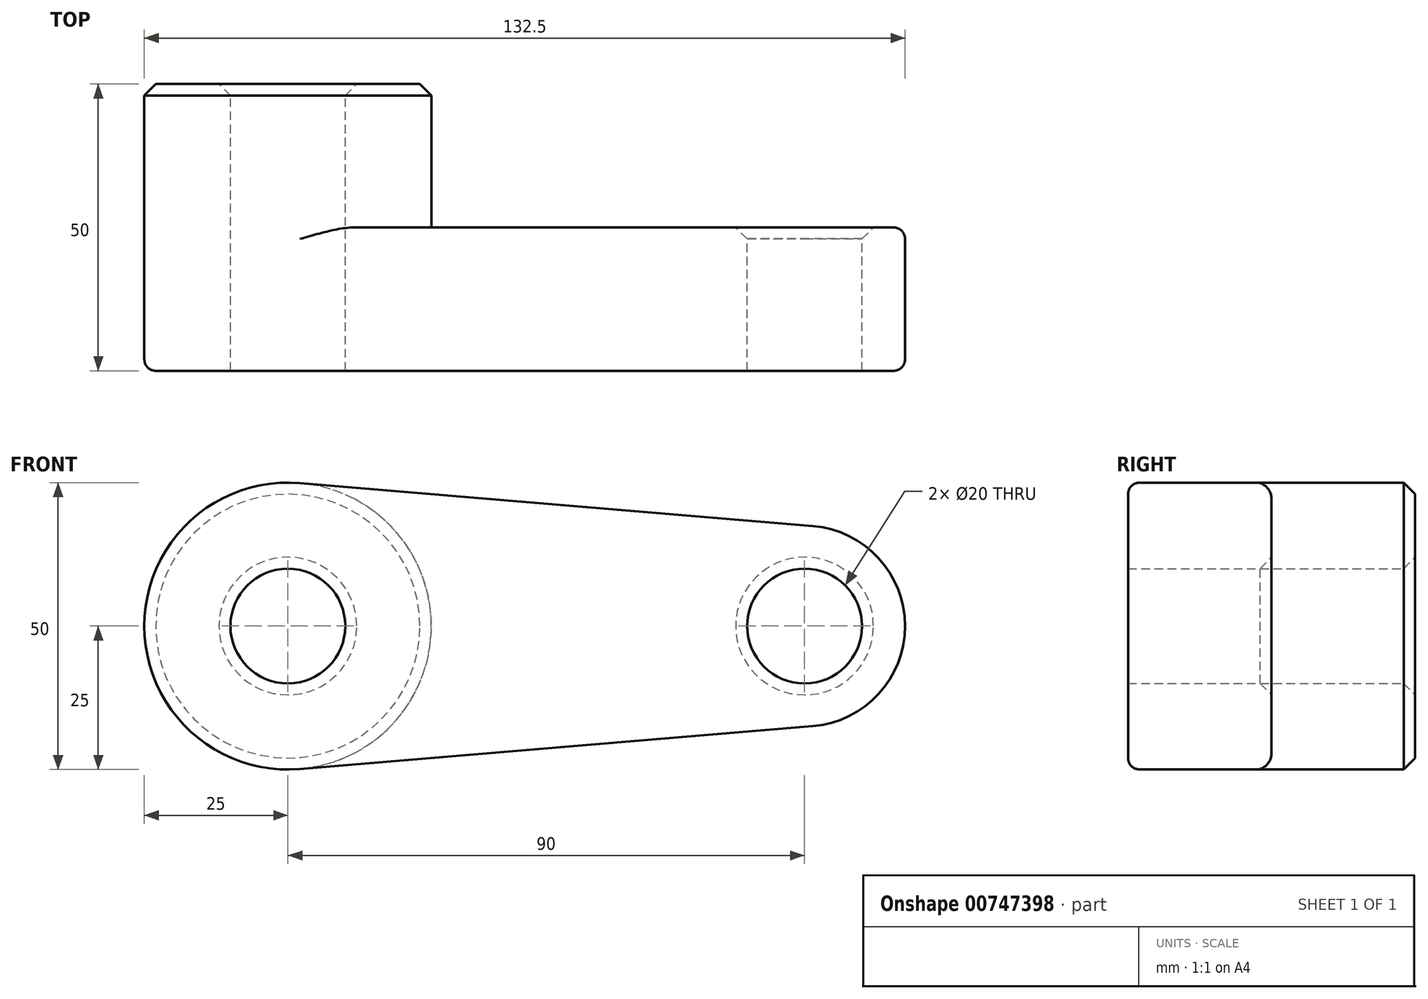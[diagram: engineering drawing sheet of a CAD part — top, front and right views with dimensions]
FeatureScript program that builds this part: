
annotation { "Feature Type Name" : "Feature", "Feature Type Description" : "" }
export const myFeature = defineFeature(function(context is Context, id is Id, definition is map)
    precondition{}
    {
        {
            var Q0;
            Q0=qCreatedBy(makeId("Front.planeOp"),FACE);
            var sketch = newSketch(context, id + "F0", { "sketchPlane" : qUnion([Q0])});
            skCircle(sketch, "E0", {"center": v(0, 0) * mm, "radius": 25 * mm});
            skCircle(sketch, "E1", {"center": v(90, 0) * mm, "radius": 17.5 * mm});
            skLineSegment(sketch, "E2", {"start": v(2.08, 24.91) * mm, "end": v(91.46, 17.44) * mm});
            skLineSegment(sketch, "E3", {"start": v(2.08, -24.91) * mm, "end": v(91.46, -17.44) * mm});
            skCircle(sketch, "E4", {"center": v(0, 0) * mm, "radius": 10 * mm});
            skCircle(sketch, "E5", {"center": v(90, 0) * mm, "radius": 10 * mm});
            skSolve(sketch);
        }
        {
            var Q0;
            Q0 = qSketchRegion(id + "F0", true);
            extrude(context, id + "F1", {"entities" : qUnion([Q0]), "depth" : 25 * mm, "offsetDistance" : 25 * mm});
        }
        {
            var Q0;
            Q0=makeQuery(id+"F0.imprint","IMPRINT",FACE,{"disambiguationData":[TD([[makeQuery(id+"F0.imprint","IMPRINT",EDGE,{"derivedFrom":sQuery(id+"F0.wireOp",EDGE,"E4")}),-1.0]])]});
            extrude(context, id + "F2", {"entities" : qUnion([Q0]), "operationType" : NewBodyOperationType.ADD, "oppositeDirection" : true, "depth" : 25 * mm, "offsetDistance" : 25 * mm});
        }
        {
            var Q0;
            Q0=makeQuery(id+"F2.opExtrude","CAP_EDGE",EDGE,{"disambiguationData":[OSD([sQuery(id+"F0.wireOp",EDGE,"E0")])],"isStart":false});
            var Q1;
            Q1=makeQuery(id+"F2.opExtrude","CAP_EDGE",EDGE,{"disambiguationData":[OSD([sQuery(id+"F0.wireOp",EDGE,"E4")])],"isStart":false});
            var Q2;
            Q2=makeQuery(id+"F1.opExtrude","CAP_EDGE",EDGE,{"disambiguationData":[OSD([sQuery(id+"F0.wireOp",EDGE,"E5")])],"isStart":true});
            chamfer(context, id + "F3", {"entities" : qUnion([Q0, Q1, Q2]), "width" : 2 * mm, "tangentPropagation" : true});
        }
        {
            var Q0;
            Q0=makeQuery(id+"F1.opExtrude","CAP_EDGE",EDGE,{"disambiguationData":[OSD([sQuery(id+"F0.wireOp",EDGE,"E3")])],"isStart":true});
            var Q1;
            Q1=makeQuery(id+"F2.opExtrude","CAP_EDGE",EDGE,{"disambiguationData":[OSD([sQuery(id+"F0.wireOp",EDGE,"E0")])],"isStart":true});
            var Q2;
            Q2=makeQuery(id+"F1.opExtrude","CAP_EDGE",EDGE,{"disambiguationData":[OSD([sQuery(id+"F0.wireOp",EDGE,"E3")])],"isStart":false});
            fillet(context, id + "F4", {"entities" : qUnion([Q0, Q1, Q2]), "radius" : 2 * mm, "tangentPropagation" : true, "allowEdgeOverflow" : false});
        }
    });
